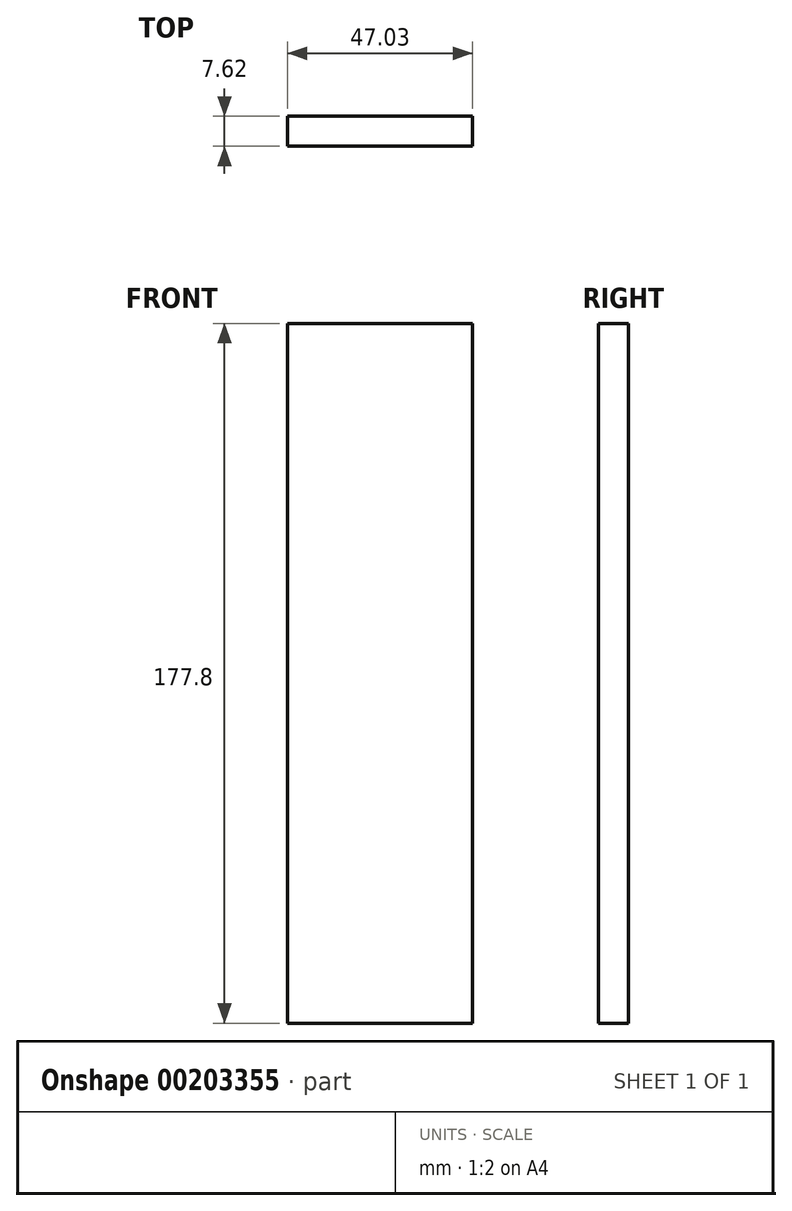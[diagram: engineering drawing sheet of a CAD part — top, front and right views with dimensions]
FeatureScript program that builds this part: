
annotation { "Feature Type Name" : "Feature", "Feature Type Description" : "" }
export const myFeature = defineFeature(function(context is Context, id is Id, definition is map)
    precondition{}
    {
        {
            var Q0;
            Q0=qCreatedBy(makeId("Front.planeOp"),FACE);
            var sketch = newSketch(context, id + "F0", { "sketchPlane" : qUnion([Q0])});
            skLineSegment(sketch, "E0.bottom", {"start": v(17.94, 81.74) * mm, "end": v(64.97, 81.74) * mm});
            skLineSegment(sketch, "E0.top", {"start": v(17.94, -96.06) * mm, "end": v(64.97, -96.06) * mm});
            skLineSegment(sketch, "E0.left", {"start": v(17.94, 81.74) * mm, "end": v(17.94, -96.06) * mm});
            skLineSegment(sketch, "E0.right", {"start": v(64.97, 81.74) * mm, "end": v(64.97, -96.06) * mm});
            skSolve(sketch);
        }
        {
            var Q0;
            Q0 = qSketchRegion(id + "F0", true);
            extrude(context, id + "F1", {"entities" : qUnion([Q0]), "depth" : 7.62 * mm});
        }
    });
